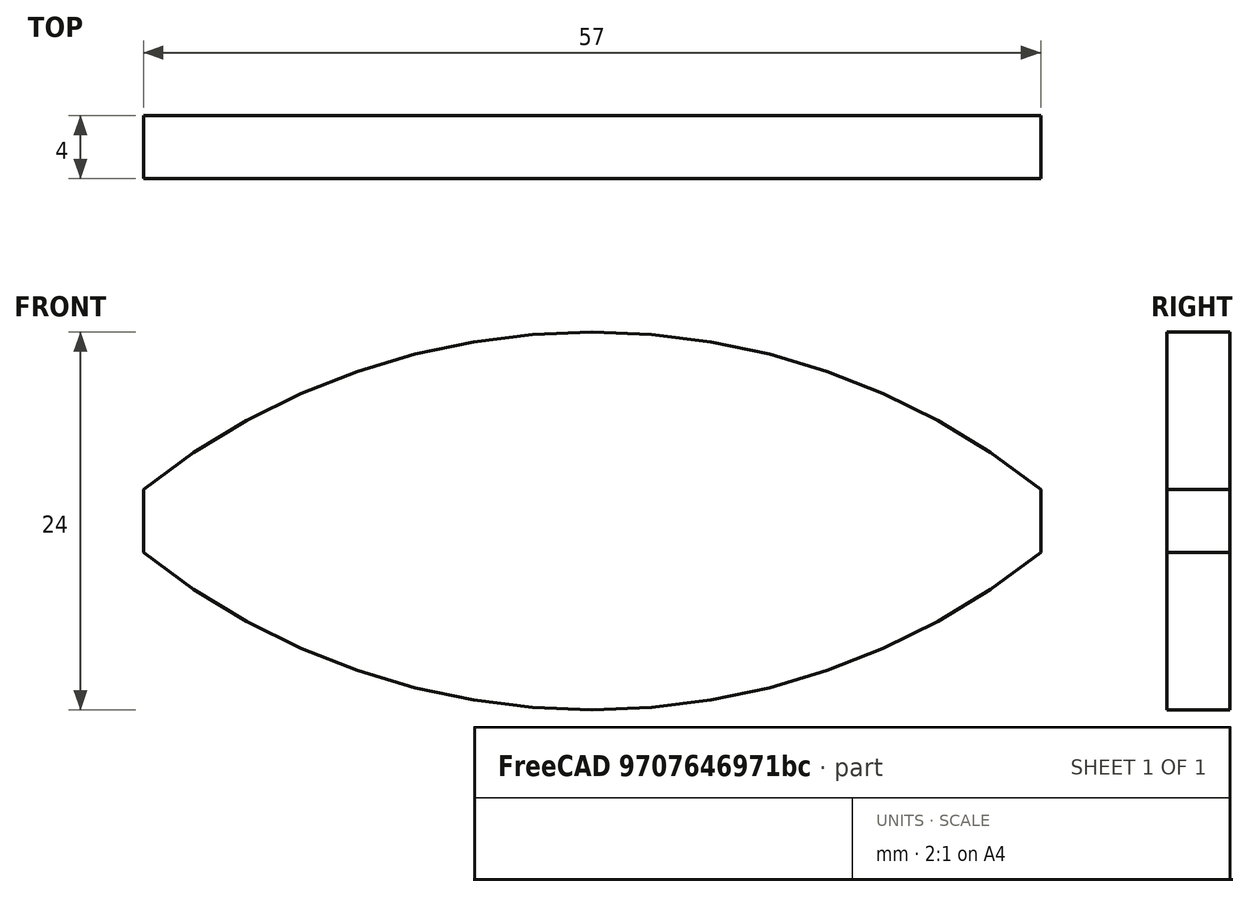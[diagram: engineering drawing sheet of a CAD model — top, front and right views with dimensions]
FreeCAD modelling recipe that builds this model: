
FCSTD DOCUMENT  (FreeCAD 1.1R20260325 (Git shallow))
Label: Biscuits_4_x_24_x_57_mm
License: All rights reserved
LicenseURL: http://en.wikipedia.org/wiki/All_rights_reserved
objects: App::LinkGroup×2, App::Point×2, Sketcher::SketchObject×1, Spreadsheet::Sheet×1, PartDesign::Pad×1, PartDesign::Body×1, App::Part×1
note: 6 computed .brp shape members not serialized (recipe doc carries the construction recipe); baked Part::Feature solids carry a one-line shape summary decoded from their .brp

FEATURE [Sketcher::SketchObject] Sketch
  ArcFitTolerance = 0
  AttachmentSupport = -> [XZ_Plane001]
  ExternalTypes = [0]
  FullyConstrained = false
  MakeInternals = false
  MapMode = 5
  Placement = pos=(0,0,0) rot=(1,0,0;1.5708rad)
  _ExternalGeoVersion = 0
  expr: Constraints[13] = <<settings>>.bw
  expr: Constraints[14] = <<settings>>.bh
  expr: Constraints[16] = <<settings>>.bw / 2
  sketch-geometry (6):
    g0: LineSegment StartX=-28.5 StartY=14 StartZ=0 EndX=-28.5 EndY=10 EndZ=0
    g1: LineSegment StartX=28.5 StartY=14 StartZ=0 EndX=28.5 EndY=10 EndZ=0
    g2: ArcOfCircle CenterX=0 CenterY=-21.6125 CenterZ=0 NormalX=0 NormalY=0 NormalZ=1 AngleXU=0 Radius=45.6125 StartAngle=0.895884 EndAngle=2.24571
    g3: ArcOfCircle CenterX=0 CenterY=45.6125 CenterZ=0 NormalX=0 NormalY=0 NormalZ=1 AngleXU=0 Radius=45.6125 StartAngle=4.03748 EndAngle=5.3873
    g4: LineSegment [constr] StartX=0 StartY=24 StartZ=0 EndX=0 EndY=0 EndZ=0
    g5: LineSegment [constr] StartX=-49.5813 StartY=12 StartZ=0 EndX=66.2857 EndY=12 EndZ=0
  constraints (18):
    c: Vertical(g0)
    c: Vertical(g1)
    c: Coincident(g2,g0)
    c: Coincident(g2,g1)
    c: Coincident(g3,g0)
    c: Coincident(g3,g1)
    c: PointOnObject(g4,g2)
    c: PointOnObject(g4,g3)
    c: Vertical(g4)
    c: Coincident(g4,g-1)
    c: Horizontal(g1,g0)
    c: DistanceY(g1,g1) = 4
    c: Vertical(g3,g4)
    c: DistanceY(g4,g4) = 24
    c: DistanceX(g0,g1) = 57
    c: Horizontal(g5)
    c: DistanceY(g4,g5) = 12
    c: Symmetric(g2,g3,g5)
FEATURE [Spreadsheet::Sheet] Spreadsheet  label="settings"
  cells = A1='Settings:; A2='Width; B2(bw)=24; A3='Height; B3(bh)=57
FEATURE [PartDesign::Pad] Pad
  Direction = (0,-1,2e-16)
  Length = 4
  Length2 = 10
  Placement = pos=(0,0,0) rot=(1,0,0;1.5708rad)
  Profile = -> Sketch
  ReferenceAxis = -> Sketch [N_Axis]
  SideType = 0
  Suppressed = false
  Type = 0
  Type2 = 0
FEATURE [PartDesign::Body] Body
  AllowCompound = true
  Group = -> [Sketch,Pad]
  Origin = -> Origin001
  Placement = pos=(0,2,0) rot=(0,0,1;0rad)
  Tip = -> Pad
FEATURE [App::Part] Part
  Group = -> [Body]
  Origin = -> Origin
FEATURE [App::LinkGroup] LinkGroup  label="Biscuits 4 x 24 x 57 mm, link this"
  ElementList = -> [Part]
  LinkMode = 0
FEATURE [App::LinkGroup] LinkGroup001  label="Biscuits 4 x 24 x 57 mm, hide this"
  ElementList = -> [LinkGroup]
  LinkMode = 0
FEATURE [App::Point] Origin002  label="Origin"
  Role = Origin
FEATURE [App::Point] Origin003  label="Origin"
  Role = Origin
